# Revit family: Table-Allermuir-Pause-PST167L-PST227L
name_source: partatom
category: Furniture
revit_build: Autodesk Revit Architecture 2012 (Build: 20110309_2315(x64)
units: mm (PartAtom-declared; Revit-internal decimal feet)

## types (2) — shared parameters
04 CSI = 12 51 00
95 CSI = 12510
Assembly Code = E2020200
CAD Blocks URL = http://www.allermuir.net
Color Availability = See price list for material options
Fabric Spec Sheets = http://www.allermuir.net
LEED Stats URL = http://www.allermuir.net
Leg Base = Plastic - Allermuir - Black
Legs = Metal - Allermuir - Silver
Manufacturer = Allermuir
Manufacturer Fax = (419) 887 5805
Model = PST167L
Overall Height = 2' - 5 1/8"
Plastic Arms in Black = No
Plugin Data URL = http://products.ecoscorecard.com
Pricing URL = http://www.allermuir.net
Product Line = Pause Tables
Product Page URL = http://www.allermuir.net
Specifications URL = http://www.allermuir.net
Stacks = No
Subcategory = Tables
Table Top = Laminate - Allermuir - White
URL = http://www.allermuir.net
Upholstered Back = No
Upholstered Seat = No
Weight = 15.0 lb
ecoScorecard Product Page = http://products.ecoscorecard.com
ecoScorecard_data = http://thesenatorgroup.ecoscorecard.com

## per-type parameters (varying)
| type | Overall Depth | Overall Width |
| PST227L | 2' - 5 17/32" | 7' - 2 5/8" |
| PST167L | 2' - 5 1/8" | 5' - 3" |

## geometry (parser evidence)
native form markers: Blend x15, Sweep x6
no freeform markers — native parametric forms only
